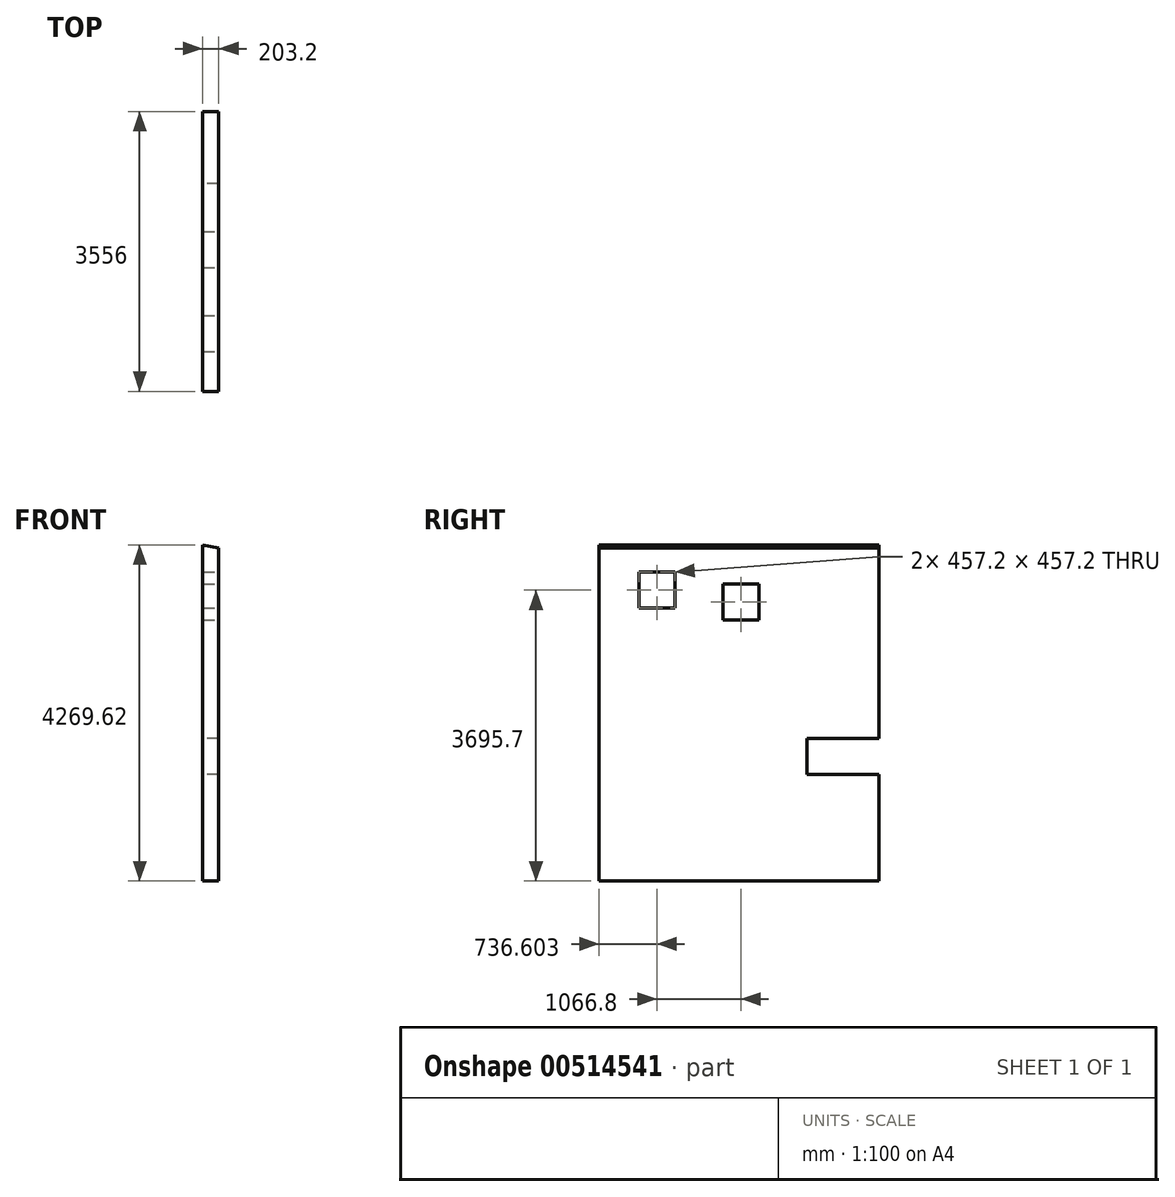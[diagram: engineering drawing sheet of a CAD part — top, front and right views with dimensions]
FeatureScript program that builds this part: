
annotation { "Feature Type Name" : "Feature", "Feature Type Description" : "" }
export const myFeature = defineFeature(function(context is Context, id is Id, definition is map)
    precondition{}
    {
        {
            var Q0;
            Q0=qCreatedBy(makeId("Right.planeOp"),FACE);
            var sketch = newSketch(context, id + "F0", { "sketchPlane" : qUnion([Q0])});
            skLineSegment(sketch, "E0.bottom", {"start": v(1780.41, 2353.82) * mm, "end": v(-1775.59, 2353.82) * mm});
            skLineSegment(sketch, "E0.top", {"start": v(1780.41, -2353.82) * mm, "end": v(-1775.59, -2353.82) * mm});
            skLineSegment(sketch, "E0.left", {"start": v(1780.41, 2353.82) * mm, "end": v(1780.41, -2353.82) * mm});
            skLineSegment(sketch, "E0.right", {"start": v(-1775.59, 2353.82) * mm, "end": v(-1775.59, -2353.82) * mm});
            skPoint(sketch, "E0.middle", {"position": v(2.41, 0) * mm});
            skSolve(sketch);
        }
        {
            var Q0;
            Q0=makeQuery(id+"F0.imprint","IMPRINT",FACE,{"disambiguationData":[TD([[makeQuery(id+"F0.imprint","IMPRINT",EDGE,{"derivedFrom":sQuery(id+"F0.wireOp",EDGE,"E0.bottom")}),1.0]])]});
            extrude(context, id + "F1", {"entities" : qUnion([Q0]), "depth" : 203.2 * mm, "offsetDistance" : 25.4 * mm});
        }
        {
            var Q0;
            Q0=makeQuery(id+"F1.opExtrude","SWEPT_FACE",FACE,{"disambiguationData":[OSD([sQuery(id+"F0.wireOp",EDGE,"E0.right")])]});
            var sketch = newSketch(context, id + "F2", { "sketchPlane" : qUnion([Q0])});
            skLineSegment(sketch, "E1", {"start": v(1626.52, 1591.45) * mm, "end": v(0, 1915.8) * mm});
            skLineSegment(sketch, "E2", {"start": v(1626.52, 1591.45) * mm, "end": v(0, 1591.45) * mm});
            skLineSegment(sketch, "E3", {"start": v(0, 1915.8) * mm, "end": v(0, 1591.45) * mm});
            skLineSegment(sketch, "E4", {"start": v(0, 1591.45) * mm, "end": v(0, 1591.45) * mm});
            skLineSegment(sketch, "E5", {"start": v(203.2, -2353.82) * mm, "end": v(203.2, 1875.28) * mm});
            skSolve(sketch);
        }
        {
            var Q0;
            {var subQ1=sQuery(id+"F0.wireOp",EDGE,"E0.right");var subQ6=makeQuery(id+"F1.opExtrude","SWEPT_EDGE",EDGE,{"disambiguationData":[OSD([sQuery(id+"F0.wireOp",EDGE,"E0.bottom"),subQ1])]});Q0=makeQuery(id+"F2.imprint","IMPRINT",FACE,{"disambiguationData":[TD([[makeQuery(id+"F2.imprint","IMPRINT",EDGE,{"derivedFrom":subQ6}),1.0]])]});}
            extrude(context, id + "F3", {"entities" : qUnion([Q0]), "operationType" : NewBodyOperationType.REMOVE, "oppositeDirection" : true, "depth" : 3556 * mm, "offsetDistance" : 25.4 * mm});
        }
        {
            var Q0;
            Q0=makeQuery(id+"F1.opExtrude","CAP_FACE",FACE,{"disambiguationData":[OSD([sQuery(id+"F0.wireOp",EDGE,"E0.bottom"),sQuery(id+"F0.wireOp",EDGE,"E0.top"),sQuery(id+"F0.wireOp",EDGE,"E0.left"),sQuery(id+"F0.wireOp",EDGE,"E0.right")])],"isStart":true});
            var sketch = newSketch(context, id + "F4", { "sketchPlane" : qUnion([Q0])});
            skLineSegment(sketch, "E6", {"start": v(-1780.41, -2353.82) * mm, "end": v(-1780.41, -2068.07) * mm});
            skLineSegment(sketch, "E7", {"start": v(-1780.41, -2068.07) * mm, "end": v(-1780.41, -1153.67) * mm});
            skLineSegment(sketch, "E8", {"start": v(-1780.41, -1153.67) * mm, "end": v(-1780.41, -1001.27) * mm});
            skLineSegment(sketch, "E9.bottom", {"start": v(-1780.41, -1001.27) * mm, "end": v(-866.01, -1001.27) * mm});
            skLineSegment(sketch, "E9.top", {"start": v(-1780.41, -544.07) * mm, "end": v(-866.01, -544.07) * mm});
            skLineSegment(sketch, "E9.left", {"start": v(-1780.41, -1001.27) * mm, "end": v(-1780.41, -544.07) * mm});
            skLineSegment(sketch, "E9.right", {"start": v(-866.01, -1001.27) * mm, "end": v(-866.01, -544.07) * mm});
            skSolve(sketch);
        }
        {
            var Q0;
            Q0=makeQuery(id+"F4.imprint","IMPRINT",FACE,{"disambiguationData":[TD([[makeQuery(id+"F4.imprint","IMPRINT",EDGE,{"derivedFrom":sQuery(id+"F4.wireOp",EDGE,"E9.bottom")}),1.0]])]});
            extrude(context, id + "F5", {"entities" : qUnion([Q0]), "operationType" : NewBodyOperationType.REMOVE, "oppositeDirection" : true, "depth" : 203.2 * mm, "offsetDistance" : 25.4 * mm});
        }
        {
            var Q0;
            Q0=makeQuery(id+"F1.opExtrude","CAP_FACE",FACE,{"disambiguationData":[OSD([sQuery(id+"F0.wireOp",EDGE,"E0.bottom"),sQuery(id+"F0.wireOp",EDGE,"E0.top"),sQuery(id+"F0.wireOp",EDGE,"E0.left"),sQuery(id+"F0.wireOp",EDGE,"E0.right")])],"isStart":false});
            var sketch = newSketch(context, id + "F6", { "sketchPlane" : qUnion([Q0])});
            skLineSegment(sketch, "E10", {"start": v(-1267.59, -2353.82) * mm, "end": v(-1267.59, -2068.07) * mm});
            skLineSegment(sketch, "E11", {"start": v(-1267.59, -2068.07) * mm, "end": v(-1267.59, -239.27) * mm});
            skLineSegment(sketch, "E12", {"start": v(-1267.59, -239.27) * mm, "end": v(-1267.59, 46.48) * mm});
            skLineSegment(sketch, "E13", {"start": v(-1267.59, 46.48) * mm, "end": v(-1267.59, 1113.28) * mm});
            skLineSegment(sketch, "E14.bottom", {"start": v(-1267.59, 1113.28) * mm, "end": v(-810.39, 1113.28) * mm});
            skLineSegment(sketch, "E14.top", {"start": v(-1267.59, 1570.48) * mm, "end": v(-810.39, 1570.48) * mm});
            skLineSegment(sketch, "E14.left", {"start": v(-1267.59, 1113.28) * mm, "end": v(-1267.59, 1570.48) * mm});
            skLineSegment(sketch, "E14.right", {"start": v(-810.39, 1113.28) * mm, "end": v(-810.39, 1570.48) * mm});
            skSolve(sketch);
        }
        {
            var Q0;
            Q0=makeQuery(id+"F6.imprint","IMPRINT",FACE,{"disambiguationData":[TD([[makeQuery(id+"F6.imprint","IMPRINT",EDGE,{"derivedFrom":sQuery(id+"F6.wireOp",EDGE,"E14.bottom")}),1.0]])]});
            extrude(context, id + "F7", {"entities" : qUnion([Q0]), "operationType" : NewBodyOperationType.REMOVE, "oppositeDirection" : true, "depth" : 203.2 * mm, "offsetDistance" : 25.4 * mm});
        }
        {
            var Q0;
            Q0=makeQuery(id+"F1.opExtrude","CAP_FACE",FACE,{"disambiguationData":[OSD([sQuery(id+"F0.wireOp",EDGE,"E0.bottom"),sQuery(id+"F0.wireOp",EDGE,"E0.top"),sQuery(id+"F0.wireOp",EDGE,"E0.left"),sQuery(id+"F0.wireOp",EDGE,"E0.right")])],"isStart":false});
            var sketch = newSketch(context, id + "F8", { "sketchPlane" : qUnion([Q0])});
            skLineSegment(sketch, "E15", {"start": v(-810.39, 1570.48) * mm, "end": v(-810.39, 1113.28) * mm});
            skLineSegment(sketch, "E16", {"start": v(-810.39, 1113.28) * mm, "end": v(-200.79, 1113.28) * mm});
            skLineSegment(sketch, "E17.bottom", {"start": v(-200.79, 960.88) * mm, "end": v(256.41, 960.88) * mm});
            skLineSegment(sketch, "E17.top", {"start": v(-200.79, 1418.08) * mm, "end": v(256.41, 1418.08) * mm});
            skLineSegment(sketch, "E17.left", {"start": v(-200.79, 960.88) * mm, "end": v(-200.79, 1418.08) * mm});
            skLineSegment(sketch, "E17.right", {"start": v(256.41, 960.88) * mm, "end": v(256.41, 1418.08) * mm});
            skLineSegment(sketch, "E18", {"start": v(-200.79, 1418.08) * mm, "end": v(-200.79, 1875.28) * mm});
            skSolve(sketch);
        }
        {
            var Q0;
            Q0=makeQuery(id+"F8.imprint","IMPRINT",FACE,{"disambiguationData":[TD([[makeQuery(id+"F8.imprint","IMPRINT",EDGE,{"derivedFrom":sQuery(id+"F8.wireOp",EDGE,"E17.bottom")}),1.0]])]});
            extrude(context, id + "F9", {"entities" : qUnion([Q0]), "operationType" : NewBodyOperationType.REMOVE, "oppositeDirection" : true, "depth" : 203.2 * mm, "offsetDistance" : 25.4 * mm});
        }
    });
